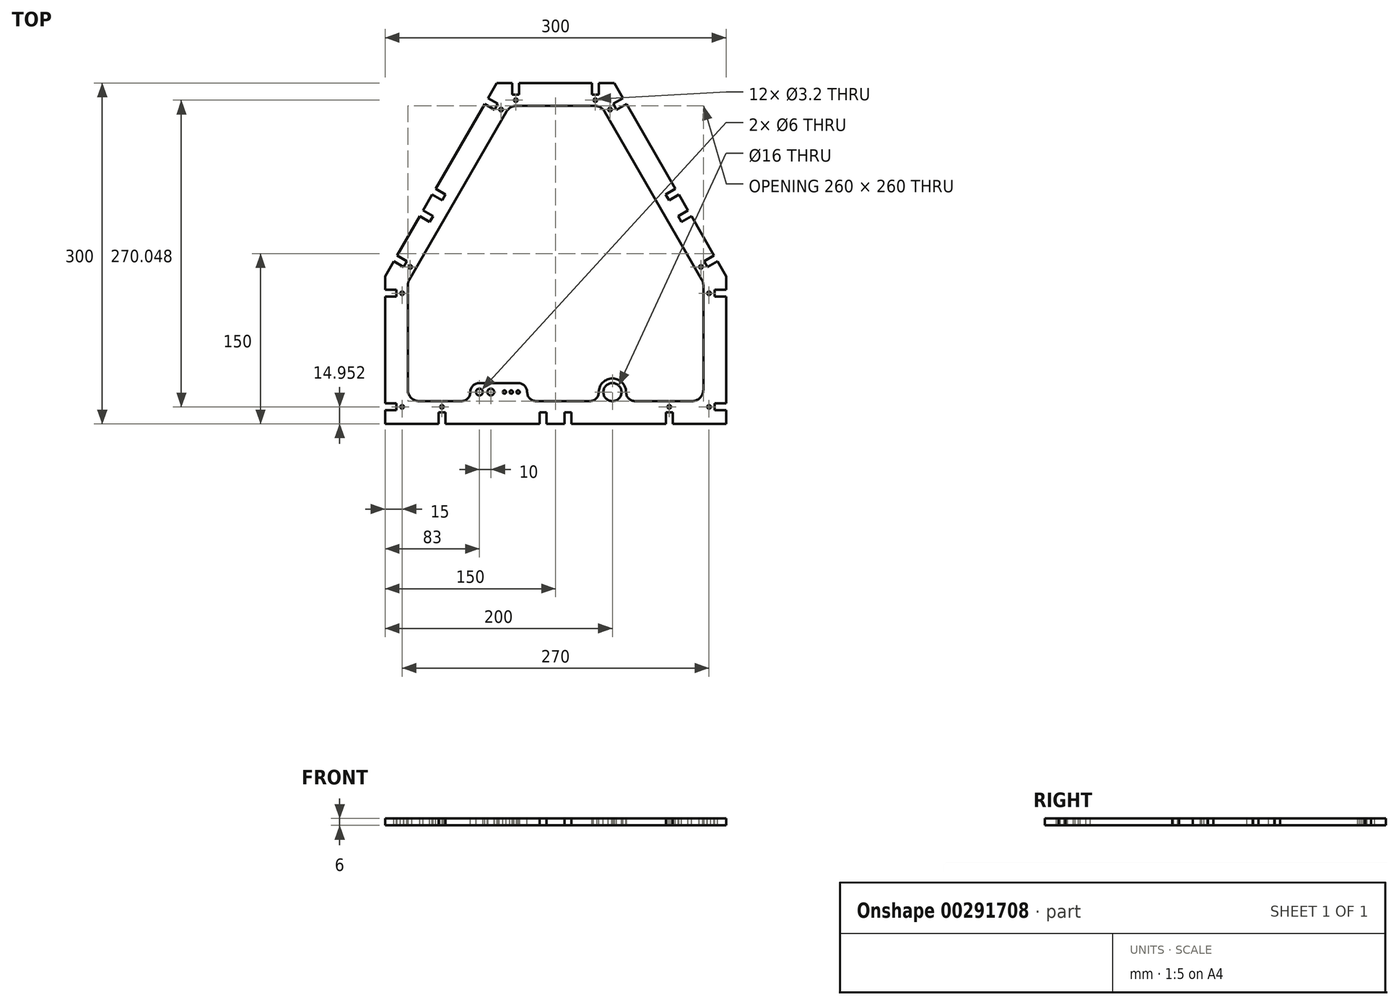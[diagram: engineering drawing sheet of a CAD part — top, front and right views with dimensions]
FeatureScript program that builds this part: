
annotation { "Feature Type Name" : "Feature", "Feature Type Description" : "" }
export const myFeature = defineFeature(function(context is Context, id is Id, definition is map)
    precondition{}
    {
        {
            var Q0;
            Q0=qCreatedBy(makeId("Top.planeOp"),FACE);
            var sketch = newSketch(context, id + "F0", { "sketchPlane" : qUnion([Q0])});
            skLineSegment(sketch, "E0.bottom", {"start": v(150, -150) * mm, "end": v(-150, -150) * mm});
            skLineSegment(sketch, "E0.top", {"start": v(150, 150) * mm, "end": v(-150, 150) * mm, "construction": true});
            skLineSegment(sketch, "E0.left", {"start": v(150, -150) * mm, "end": v(150, 150) * mm, "construction": true});
            skLineSegment(sketch, "E0.right", {"start": v(-150, -150) * mm, "end": v(-150, 150) * mm, "construction": true});
            skPoint(sketch, "E0.middle", {"position": v(0, 0) * mm});
            skLineSegment(sketch, "E1", {"start": v(-225, -150) * mm, "end": v(225, -150) * mm, "construction": true});
            skLineSegment(sketch, "E2", {"start": v(225, -150) * mm, "end": v(0, 239.71) * mm, "construction": true});
            skLineSegment(sketch, "E3", {"start": v(0, 239.71) * mm, "end": v(-225, -150) * mm, "construction": true});
            skLineSegment(sketch, "E4", {"start": v(-150, -150) * mm, "end": v(-150, -20.1) * mm});
            skLineSegment(sketch, "E5", {"start": v(-150, -20.1) * mm, "end": v(-51.8, 150) * mm});
            skLineSegment(sketch, "E6", {"start": v(-51.8, 150) * mm, "end": v(51.8, 150) * mm});
            skLineSegment(sketch, "E7", {"start": v(51.8, 150) * mm, "end": v(150, -20.1) * mm});
            skLineSegment(sketch, "E8", {"start": v(150, -20.1) * mm, "end": v(150, -150) * mm});
            skSolve(sketch);
        }
        {
            var Q0;
            Q0=makeQuery(id+"F0.imprint","IMPRINT",FACE,{"disambiguationData":[TD([[makeQuery(id+"F0.imprint","IMPRINT",EDGE,{"derivedFrom":sQuery(id+"F0.wireOp",EDGE,"E0.bottom")}),-1.0]])]});
            extrude(context, id + "F1", {"entities" : qUnion([Q0]), "depth" : 6 * mm});
        }
        {
            var Q0;
            Q0=makeQuery(id+"F1.opExtrude","CAP_FACE",FACE,{"disambiguationData":[OSD([sQuery(id+"F0.wireOp",EDGE,"E0.bottom"),sQuery(id+"F0.wireOp",EDGE,"E4"),sQuery(id+"F0.wireOp",EDGE,"E5"),sQuery(id+"F0.wireOp",EDGE,"E6"),sQuery(id+"F0.wireOp",EDGE,"E7"),sQuery(id+"F0.wireOp",EDGE,"E8")])],"isStart":false});
            var sketch = newSketch(context, id + "F2", { "sketchPlane" : qUnion([Q0])});
            skLineSegment(sketch, "E9", {"start": v(-100.9, 64.95) * mm, "end": v(0, 6.7) * mm, "construction": true});
            skLineSegment(sketch, "E10", {"start": v(100.9, 64.95) * mm, "end": v(0, 6.7) * mm, "construction": true});
            skLineSegment(sketch, "E11", {"start": v(0, -150) * mm, "end": v(0, 6.7) * mm, "construction": true});
            skLineSegment(sketch, "E12", {"start": v(-150, -85.05) * mm, "end": v(150, -85.05) * mm, "construction": true});
            skLineSegment(sketch, "E13", {"start": v(-142.4, -6.93) * mm, "end": v(-139.4, -1.73) * mm});
            skLineSegment(sketch, "E14", {"start": v(-139.4, -1.73) * mm, "end": v(-130.74, -6.73) * mm});
            skLineSegment(sketch, "E15", {"start": v(-130.74, -6.73) * mm, "end": v(-133.74, -11.93) * mm});
            skLineSegment(sketch, "E16", {"start": v(-133.74, -11.93) * mm, "end": v(-142.4, -6.93) * mm});
            skLineSegment(sketch, "E17", {"start": v(-140.9, -4.33) * mm, "end": v(-127.9, -11.83) * mm, "construction": true});
            skCircle(sketch, "E18", {"center": v(-127.9, -11.83) * mm, "radius": 1.6 * mm});
            skLineSegment(sketch, "E19.MirrorCS", {"start": v(-59.4, 136.83) * mm, "end": v(-62.4, 131.64) * mm});
            skCircle(sketch, "E20.MirrorC", {"center": v(-47.9, 126.73) * mm, "radius": 1.6 * mm});
            skLineSegment(sketch, "E21.MirrorCS", {"start": v(-50.74, 131.83) * mm, "end": v(-59.4, 136.83) * mm});
            skLineSegment(sketch, "E22.MirrorCS", {"start": v(-62.4, 131.64) * mm, "end": v(-53.74, 126.64) * mm});
            skLineSegment(sketch, "E23.MirrorCS", {"start": v(-53.74, 126.64) * mm, "end": v(-50.74, 131.83) * mm});
            skLineSegment(sketch, "E24.MirrorCS", {"start": v(142.4, -6.93) * mm, "end": v(139.4, -1.73) * mm});
            skLineSegment(sketch, "E25.MirrorCS", {"start": v(139.4, -1.73) * mm, "end": v(130.74, -6.73) * mm});
            skLineSegment(sketch, "E26.MirrorCS", {"start": v(130.74, -6.73) * mm, "end": v(133.74, -11.93) * mm});
            skLineSegment(sketch, "E27.MirrorCS", {"start": v(133.74, -11.93) * mm, "end": v(142.4, -6.93) * mm});
            skCircle(sketch, "E28.MirrorC", {"center": v(127.9, -11.83) * mm, "radius": 1.6 * mm});
            skLineSegment(sketch, "E29.MirrorCS", {"start": v(62.4, 131.64) * mm, "end": v(53.74, 126.64) * mm});
            skLineSegment(sketch, "E30.MirrorCS", {"start": v(59.4, 136.83) * mm, "end": v(62.4, 131.64) * mm});
            skLineSegment(sketch, "E31.MirrorCS", {"start": v(53.74, 126.64) * mm, "end": v(50.74, 131.83) * mm});
            skLineSegment(sketch, "E32.MirrorCS", {"start": v(50.74, 131.83) * mm, "end": v(59.4, 136.83) * mm});
            skCircle(sketch, "E33.MirrorC", {"center": v(47.9, 126.73) * mm, "radius": 1.6 * mm});
            skLineSegment(sketch, "E34.bottom", {"start": v(-150, -32.05) * mm, "end": v(-140, -32.05) * mm});
            skLineSegment(sketch, "E34.top", {"start": v(-150, -38.05) * mm, "end": v(-140, -38.05) * mm});
            skLineSegment(sketch, "E34.left", {"start": v(-150, -32.05) * mm, "end": v(-150, -38.05) * mm});
            skLineSegment(sketch, "E34.right", {"start": v(-140, -32.05) * mm, "end": v(-140, -38.05) * mm});
            skLineSegment(sketch, "E35", {"start": v(-150, -35.05) * mm, "end": v(-135, -35.05) * mm, "construction": true});
            skCircle(sketch, "E36", {"center": v(-135, -35.05) * mm, "radius": 1.6 * mm});
            skLineSegment(sketch, "E37.MirrorCS", {"start": v(-150, -138.05) * mm, "end": v(-150, -132.05) * mm});
            skLineSegment(sketch, "E38.MirrorCS", {"start": v(-150, -132.05) * mm, "end": v(-140, -132.05) * mm});
            skCircle(sketch, "E39.MirrorC", {"center": v(-135, -135.05) * mm, "radius": 1.6 * mm});
            skLineSegment(sketch, "E40.MirrorCS", {"start": v(-140, -138.05) * mm, "end": v(-140, -132.05) * mm});
            skLineSegment(sketch, "E41.MirrorCS", {"start": v(-150, -138.05) * mm, "end": v(-140, -138.05) * mm});
            skLineSegment(sketch, "E42.MirrorCS", {"start": v(-150, -135.05) * mm, "end": v(-135, -135.05) * mm, "construction": true});
            skLineSegment(sketch, "E43.MirrorCS", {"start": v(140, -138.05) * mm, "end": v(140, -132.05) * mm});
            skLineSegment(sketch, "E44.MirrorCS", {"start": v(150, -138.05) * mm, "end": v(150, -132.05) * mm});
            skCircle(sketch, "E45.MirrorC", {"center": v(135, -135.05) * mm, "radius": 1.6 * mm});
            skLineSegment(sketch, "E46.MirrorCS", {"start": v(150, -138.05) * mm, "end": v(140, -138.05) * mm});
            skCircle(sketch, "E47.MirrorC", {"center": v(135, -35.05) * mm, "radius": 1.6 * mm});
            skLineSegment(sketch, "E48.MirrorCS", {"start": v(150, -132.05) * mm, "end": v(140, -132.05) * mm});
            skLineSegment(sketch, "E49.MirrorCS", {"start": v(150, -32.05) * mm, "end": v(150, -38.05) * mm});
            skLineSegment(sketch, "E50.MirrorCS", {"start": v(140, -32.05) * mm, "end": v(140, -38.05) * mm});
            skLineSegment(sketch, "E51.MirrorCS", {"start": v(150, -135.05) * mm, "end": v(135, -135.05) * mm, "construction": true});
            skLineSegment(sketch, "E52.MirrorCS", {"start": v(150, -32.05) * mm, "end": v(140, -32.05) * mm});
            skLineSegment(sketch, "E53.MirrorCS", {"start": v(150, -38.05) * mm, "end": v(140, -38.05) * mm});
            skLineSegment(sketch, "E54.MirrorCS", {"start": v(150, -35.05) * mm, "end": v(135, -35.05) * mm, "construction": true});
            skLineSegment(sketch, "E55.bottom", {"start": v(-38, 150) * mm, "end": v(-32, 150) * mm});
            skLineSegment(sketch, "E55.top", {"start": v(-38, 140) * mm, "end": v(-32, 140) * mm});
            skLineSegment(sketch, "E55.left", {"start": v(-38, 150) * mm, "end": v(-38, 140) * mm});
            skLineSegment(sketch, "E55.right", {"start": v(-32, 150) * mm, "end": v(-32, 140) * mm});
            skLineSegment(sketch, "E56", {"start": v(-35, 150) * mm, "end": v(-35, 135) * mm, "construction": true});
            skCircle(sketch, "E57", {"center": v(-35, 135) * mm, "radius": 1.6 * mm});
            skLineSegment(sketch, "E58.MirrorCS", {"start": v(-32, 150) * mm, "end": v(-38, 150) * mm});
            skLineSegment(sketch, "E59.MirrorCS", {"start": v(-32, 140) * mm, "end": v(-38, 140) * mm});
            skLineSegment(sketch, "E60.MirrorCS", {"start": v(32, 150) * mm, "end": v(32, 140) * mm});
            skLineSegment(sketch, "E61.MirrorCS", {"start": v(32, 140) * mm, "end": v(38, 140) * mm});
            skCircle(sketch, "E62.MirrorC", {"center": v(35, 135) * mm, "radius": 1.6 * mm});
            skLineSegment(sketch, "E63.MirrorCS", {"start": v(38, 150) * mm, "end": v(38, 140) * mm});
            skLineSegment(sketch, "E64.MirrorCS", {"start": v(38, 150) * mm, "end": v(32, 150) * mm});
            skLineSegment(sketch, "E65.MirrorCS", {"start": v(32, 150) * mm, "end": v(38, 150) * mm});
            skLineSegment(sketch, "E66.MirrorCS", {"start": v(38, 140) * mm, "end": v(32, 140) * mm});
            skLineSegment(sketch, "E67.bottom", {"start": v(-103, -140) * mm, "end": v(-97, -140) * mm});
            skLineSegment(sketch, "E67.top", {"start": v(-103, -150) * mm, "end": v(-97, -150) * mm});
            skLineSegment(sketch, "E67.left", {"start": v(-103, -140) * mm, "end": v(-103, -150) * mm});
            skLineSegment(sketch, "E67.right", {"start": v(-97, -140) * mm, "end": v(-97, -150) * mm});
            skLineSegment(sketch, "E68", {"start": v(-100, -150) * mm, "end": v(-100, -135) * mm, "construction": true});
            skCircle(sketch, "E69", {"center": v(-100, -135) * mm, "radius": 1.6 * mm});
            skCircle(sketch, "E70.MirrorC", {"center": v(100, -135) * mm, "radius": 1.6 * mm});
            skLineSegment(sketch, "E71.MirrorCS", {"start": v(103, -150) * mm, "end": v(97, -150) * mm});
            skLineSegment(sketch, "E72.MirrorCS", {"start": v(103, -140) * mm, "end": v(97, -140) * mm});
            skLineSegment(sketch, "E73.MirrorCS", {"start": v(97, -140) * mm, "end": v(97, -150) * mm});
            skLineSegment(sketch, "E74.MirrorCS", {"start": v(103, -140) * mm, "end": v(103, -150) * mm});
            skSolve(sketch);
        }
        {
            var Q0;
            Q0=qSketchRegion(id+"F2",true);
            extrude(context, id + "F3", {"entities" : qUnion([Q0]), "operationType" : NewBodyOperationType.REMOVE, "endBound" : BoundingType.THROUGH_ALL, "oppositeDirection" : true, "depth" : 25 * mm});
        }
        {
            var Q0;
            Q0=makeQuery(id+"F1.opExtrude","CAP_FACE",FACE,{"disambiguationData":[OSD([sQuery(id+"F0.wireOp",EDGE,"E0.bottom"),sQuery(id+"F0.wireOp",EDGE,"E4"),sQuery(id+"F0.wireOp",EDGE,"E5"),sQuery(id+"F0.wireOp",EDGE,"E6"),sQuery(id+"F0.wireOp",EDGE,"E7"),sQuery(id+"F0.wireOp",EDGE,"E8")])],"isStart":false});
            var sketch = newSketch(context, id + "F4", { "sketchPlane" : qUnion([Q0])});
            skLineSegment(sketch, "E75", {"start": v(0, -150) * mm, "end": v(0, -20.1) * mm, "construction": true});
            skPoint(sketch, "E75.endSnap0", {"position": v(0, -150) * mm});
            skLineSegment(sketch, "E76", {"start": v(-112.5, 44.86) * mm, "end": v(0, -20.1) * mm, "construction": true});
            skLineSegment(sketch, "E77", {"start": v(0, -20.1) * mm, "end": v(112.5, 44.86) * mm, "construction": true});
            skLineSegment(sketch, "E78.bottom", {"start": v(-14, -140) * mm, "end": v(-8, -140) * mm});
            skLineSegment(sketch, "E78.top", {"start": v(-14, -150) * mm, "end": v(-8, -150) * mm});
            skLineSegment(sketch, "E78.left", {"start": v(-14, -140) * mm, "end": v(-14, -150) * mm});
            skLineSegment(sketch, "E78.right", {"start": v(-8, -140) * mm, "end": v(-8, -150) * mm});
            skLineSegment(sketch, "E79.MirrorCS", {"start": v(14, -140) * mm, "end": v(8, -140) * mm});
            skLineSegment(sketch, "E80.MirrorCS", {"start": v(14, -150) * mm, "end": v(8, -150) * mm});
            skLineSegment(sketch, "E81.MirrorCS", {"start": v(8, -140) * mm, "end": v(8, -150) * mm});
            skLineSegment(sketch, "E82.MirrorCS", {"start": v(14, -140) * mm, "end": v(14, -150) * mm});
            skLineSegment(sketch, "E83", {"start": v(-116.5, 37.93) * mm, "end": v(-119.5, 32.73) * mm});
            skLineSegment(sketch, "E84", {"start": v(-119.5, 32.73) * mm, "end": v(-110.84, 27.73) * mm});
            skLineSegment(sketch, "E85", {"start": v(-110.84, 27.73) * mm, "end": v(-107.84, 32.93) * mm});
            skLineSegment(sketch, "E86", {"start": v(-107.84, 32.93) * mm, "end": v(-116.5, 37.93) * mm});
            skLineSegment(sketch, "E87.MirrorCS", {"start": v(-108.5, 51.78) * mm, "end": v(-105.5, 56.98) * mm});
            skLineSegment(sketch, "E88.MirrorCS", {"start": v(-96.84, 51.98) * mm, "end": v(-99.84, 46.78) * mm});
            skLineSegment(sketch, "E89.MirrorCS", {"start": v(-99.84, 46.78) * mm, "end": v(-108.5, 51.78) * mm});
            skLineSegment(sketch, "E90.MirrorCS", {"start": v(-105.5, 56.98) * mm, "end": v(-96.84, 51.98) * mm});
            skLineSegment(sketch, "E91.MirrorCS", {"start": v(110.84, 27.73) * mm, "end": v(107.84, 32.93) * mm});
            skLineSegment(sketch, "E92.MirrorCS", {"start": v(96.84, 51.98) * mm, "end": v(99.84, 46.78) * mm});
            skLineSegment(sketch, "E93.MirrorCS", {"start": v(108.5, 51.78) * mm, "end": v(105.5, 56.98) * mm});
            skLineSegment(sketch, "E94.MirrorCS", {"start": v(116.5, 37.93) * mm, "end": v(119.5, 32.73) * mm});
            skLineSegment(sketch, "E95.MirrorCS", {"start": v(99.84, 46.78) * mm, "end": v(108.5, 51.78) * mm});
            skLineSegment(sketch, "E96.MirrorCS", {"start": v(105.5, 56.98) * mm, "end": v(96.84, 51.98) * mm});
            skLineSegment(sketch, "E97.MirrorCS", {"start": v(107.84, 32.93) * mm, "end": v(116.5, 37.93) * mm});
            skLineSegment(sketch, "E98.MirrorCS", {"start": v(119.5, 32.73) * mm, "end": v(110.84, 27.73) * mm});
            skSolve(sketch);
        }
        {
            var Q0;
            Q0=qSketchRegion(id+"F4",true);
            extrude(context, id + "F5", {"entities" : qUnion([Q0]), "operationType" : NewBodyOperationType.REMOVE, "endBound" : BoundingType.THROUGH_ALL, "oppositeDirection" : true, "depth" : 25 * mm});
        }
        {
            var Q0;
            Q0=makeQuery(id+"F1.opExtrude","CAP_FACE",FACE,{"disambiguationData":[OSD([sQuery(id+"F0.wireOp",EDGE,"E0.bottom"),sQuery(id+"F0.wireOp",EDGE,"E4"),sQuery(id+"F0.wireOp",EDGE,"E5"),sQuery(id+"F0.wireOp",EDGE,"E6"),sQuery(id+"F0.wireOp",EDGE,"E7"),sQuery(id+"F0.wireOp",EDGE,"E8")])],"isStart":false});
            var sketch = newSketch(context, id + "F6", { "sketchPlane" : qUnion([Q0])});
            skLineSegment(sketch, "E99", {"start": v(130, -130) * mm, "end": v(130, -25.46) * mm});
            skLineSegment(sketch, "E100", {"start": v(130, -25.46) * mm, "end": v(40.25, 130) * mm});
            skLineSegment(sketch, "E101", {"start": v(40.25, 130) * mm, "end": v(-40.25, 130) * mm});
            skLineSegment(sketch, "E102", {"start": v(-40.25, 130) * mm, "end": v(-130, -25.46) * mm});
            skLineSegment(sketch, "E103", {"start": v(-130, -25.46) * mm, "end": v(-130, -130) * mm});
            skLineSegment(sketch, "E104", {"start": v(130, -130) * mm, "end": v(62, -130) * mm});
            skLineSegment(sketch, "E105", {"start": v(62, -130) * mm, "end": v(62, -122) * mm});
            skArc(sketch, "E106", {"start": v(62, -122) * mm, "mid": v(50, -110) * mm, "end": v(38, -122) * mm});
            skLineSegment(sketch, "E107", {"start": v(38, -122) * mm, "end": v(38, -130) * mm});
            skLineSegment(sketch, "E108", {"start": v(38, -130) * mm, "end": v(-25, -130) * mm});
            skLineSegment(sketch, "E109", {"start": v(-75, -130) * mm, "end": v(-130, -130) * mm});
            skPoint(sketch, "E110", {"position": v(-50, -114) * mm});
            skLineSegment(sketch, "E111", {"start": v(0, 0) * mm, "end": v(0, -150) * mm, "construction": true});
            skLineSegment(sketch, "E112", {"start": v(50, -122) * mm, "end": v(50, -150) * mm, "construction": true});
            skLineSegment(sketch, "E113", {"start": v(-50, -114) * mm, "end": v(-50, -150) * mm, "construction": true});
            skLineSegment(sketch, "E114", {"start": v(-75, -114) * mm, "end": v(-25, -114) * mm});
            skLineSegment(sketch, "E115", {"start": v(-25, -114) * mm, "end": v(-25, -130) * mm});
            skLineSegment(sketch, "E116", {"start": v(-75, -114) * mm, "end": v(-75, -130) * mm});
            skSolve(sketch);
        }
        {
            var Q0;
            Q0=qSketchRegion(id+"F6",true);
            extrude(context, id + "F7", {"entities" : qUnion([Q0]), "operationType" : NewBodyOperationType.REMOVE, "endBound" : BoundingType.THROUGH_ALL, "oppositeDirection" : true, "depth" : 25 * mm});
        }
        {
            var Q0;
            Q0=makeQuery(id+"F7.boolean.opBoolean","COPY",EDGE,{"derivedFrom":makeQuery(id+"F7.opExtrude","SWEPT_EDGE",EDGE,{"disambiguationData":[OSD([sQuery(id+"F6.wireOp",EDGE,"E101"),sQuery(id+"F6.wireOp",EDGE,"E102")])]})});
            var Q1;
            Q1=makeQuery(id+"F7.boolean.opBoolean","COPY",EDGE,{"derivedFrom":makeQuery(id+"F7.opExtrude","SWEPT_EDGE",EDGE,{"disambiguationData":[OSD([sQuery(id+"F6.wireOp",EDGE,"E102"),sQuery(id+"F6.wireOp",EDGE,"E103")])]})});
            var Q2;
            Q2=makeQuery(id+"F7.boolean.opBoolean","COPY",EDGE,{"derivedFrom":makeQuery(id+"F7.opExtrude","SWEPT_EDGE",EDGE,{"disambiguationData":[OSD([sQuery(id+"F6.wireOp",EDGE,"HBlazGPT-XDi8-xlZP-MrhG-RJ2USWVtM3IV"),sQuery(id+"F6.wireOp",EDGE,"E103")])]})});
            var Q3;
            Q3=makeQuery(id+"F7.boolean.opBoolean","COPY",EDGE,{"derivedFrom":makeQuery(id+"F7.opExtrude","SWEPT_EDGE",EDGE,{"disambiguationData":[OSD([sQuery(id+"F6.wireOp",EDGE,"HBlazGPT-XDi8-xlZP-MrhG-RJ2USWVtM3IV"),sQuery(id+"F6.wireOp",EDGE,"E99")])]})});
            var Q4;
            Q4=makeQuery(id+"F7.boolean.opBoolean","COPY",EDGE,{"derivedFrom":makeQuery(id+"F7.opExtrude","SWEPT_EDGE",EDGE,{"disambiguationData":[OSD([sQuery(id+"F6.wireOp",EDGE,"E99"),sQuery(id+"F6.wireOp",EDGE,"E100")])]})});
            var Q5;
            Q5=makeQuery(id+"F7.boolean.opBoolean","COPY",EDGE,{"derivedFrom":makeQuery(id+"F7.opExtrude","SWEPT_EDGE",EDGE,{"disambiguationData":[OSD([sQuery(id+"F6.wireOp",EDGE,"E100"),sQuery(id+"F6.wireOp",EDGE,"E101")])]})});
            fillet(context, id + "F8", {"entities" : qUnion([Q0, Q1, Q2, Q3, Q4, Q5]), "radius" : 10 * mm, "tangentPropagation" : true, "allowEdgeOverflow" : false});
        }
        {
            var Q0;
            Q0=makeQuery(id+"F1.opExtrude","CAP_FACE",FACE,{"disambiguationData":[OSD([sQuery(id+"F0.wireOp",EDGE,"E0.bottom"),sQuery(id+"F0.wireOp",EDGE,"E4"),sQuery(id+"F0.wireOp",EDGE,"E5"),sQuery(id+"F0.wireOp",EDGE,"E6"),sQuery(id+"F0.wireOp",EDGE,"E7"),sQuery(id+"F0.wireOp",EDGE,"E8")])],"isStart":false});
            var sketch = newSketch(context, id + "F9", { "sketchPlane" : qUnion([Q0])});
            skLineSegment(sketch, "E117", {"start": v(-75, -122) * mm, "end": v(-25, -122) * mm, "construction": true});
            skLineSegment(sketch, "E118", {"start": v(38, -122) * mm, "end": v(62, -122) * mm, "construction": true});
            skCircle(sketch, "E119", {"center": v(50, -122) * mm, "radius": 8 * mm});
            skCircle(sketch, "E120", {"center": v(-67, -122) * mm, "radius": 3 * mm});
            skCircle(sketch, "E121", {"center": v(-57, -122) * mm, "radius": 3 * mm});
            skCircle(sketch, "E122", {"center": v(-39, -122) * mm, "radius": 1.5 * mm});
            skCircle(sketch, "E123", {"center": v(-33, -122) * mm, "radius": 1.5 * mm});
            skCircle(sketch, "E124", {"center": v(-45, -122) * mm, "radius": 1.5 * mm});
            skSolve(sketch);
        }
        {
            var Q0;
            Q0=qSketchRegion(id+"F9",true);
            extrude(context, id + "F10", {"entities" : qUnion([Q0]), "operationType" : NewBodyOperationType.REMOVE, "endBound" : BoundingType.THROUGH_ALL, "oppositeDirection" : true, "depth" : 25 * mm});
        }
        {
            var Q0;
            Q0=makeQuery(id+"F7.boolean.opBoolean","COPY",EDGE,{"derivedFrom":makeQuery(id+"F7.opExtrude","SWEPT_EDGE",EDGE,{"disambiguationData":[OSD([sQuery(id+"F6.wireOp",EDGE,"E109"),sQuery(id+"F6.wireOp",EDGE,"E116")])]})});
            var Q1;
            Q1=makeQuery(id+"F7.boolean.opBoolean","COPY",EDGE,{"derivedFrom":makeQuery(id+"F7.opExtrude","SWEPT_EDGE",EDGE,{"disambiguationData":[OSD([sQuery(id+"F6.wireOp",EDGE,"E114"),sQuery(id+"F6.wireOp",EDGE,"E116")])]})});
            var Q2;
            Q2=makeQuery(id+"F7.boolean.opBoolean","COPY",EDGE,{"derivedFrom":makeQuery(id+"F7.opExtrude","SWEPT_EDGE",EDGE,{"disambiguationData":[OSD([sQuery(id+"F6.wireOp",EDGE,"E114"),sQuery(id+"F6.wireOp",EDGE,"E115")])]})});
            var Q3;
            Q3=makeQuery(id+"F7.boolean.opBoolean","COPY",EDGE,{"derivedFrom":makeQuery(id+"F7.opExtrude","SWEPT_EDGE",EDGE,{"disambiguationData":[OSD([sQuery(id+"F6.wireOp",EDGE,"E108"),sQuery(id+"F6.wireOp",EDGE,"E115")])]})});
            var Q4;
            Q4=makeQuery(id+"F7.boolean.opBoolean","COPY",EDGE,{"derivedFrom":makeQuery(id+"F7.opExtrude","SWEPT_EDGE",EDGE,{"disambiguationData":[OSD([sQuery(id+"F6.wireOp",EDGE,"E104"),sQuery(id+"F6.wireOp",EDGE,"E105")])]})});
            var Q5;
            Q5=makeQuery(id+"F7.boolean.opBoolean","COPY",EDGE,{"derivedFrom":makeQuery(id+"F7.opExtrude","SWEPT_EDGE",EDGE,{"disambiguationData":[OSD([sQuery(id+"F6.wireOp",EDGE,"E107"),sQuery(id+"F6.wireOp",EDGE,"E108")])]})});
            fillet(context, id + "F11", {"entities" : qUnion([Q0, Q1, Q2, Q3, Q4, Q5]), "radius" : 8 * mm, "tangentPropagation" : true, "allowEdgeOverflow" : false});
        }
    });
